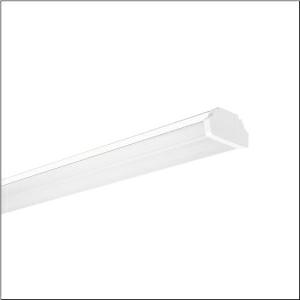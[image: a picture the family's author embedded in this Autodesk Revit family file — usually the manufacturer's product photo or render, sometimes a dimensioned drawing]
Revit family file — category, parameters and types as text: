
# Revit family: dus_r__31_mo_53bd81271v6080_96d5
name_source: partatom
category: Lighting Fixtures
units: mm (PartAtom-declared; Revit-internal decimal feet)

## family parameters
Cut with Voids When Loaded = No
Host = Face
Light Source = No
Part Type = Normal
Room Calculation Point = No
Round Connector Dimension = Use Diameter
Shared = No

## types (1)
- DUS® 31 MO (1 x LED, 7820 lm, 50.8 W, 6500K)
    Apparent Load = 51 VA
    CIE Flux Codes = 47 80 95 92 100
    Color Rendering = 80
    Color Temperature = 6500K
    Default Elevation = 1800 mm
    Description = DUS® 31 MO, luminaire insert, of sheet steel, coil coated, white, length: 1.535mm, width: 81mm, height: 90mm, 5x system unit, system units: 307mm, LED rated luminous flux: 7.820lm, light colour: 865, control gear: ON/OFF, control gear: ECG, with plug, 3-pole, with phase selection, mains connection: 220..240V, AC, 50/60Hz, rated input power: 51W, through-wiring accessed according to module size, primary optical cover: cover, of PMMA, light emission: direct distribution, primary light characteristic: symmetric, protection rating (complete): IP20, protection rating (LED compartment): IP50, insulation class (complete): insulation class I (protective earthing), certification: CE, ENEC, VDE, UKCA, impact resistance: IK03, permissible ambient temperature for indoor applications: -35..+35°C, corresponds to IFS (International Featured Standards) requirements for safety and quality in the food industry, reducing of maximum allowable ambient temperature of 5°C with ceiling mounting, packaging unit: 1 piece
    Height = 95 mm
    Lamp = 1 x LED
    Lamp Light Flux = 7820 lm
    Lamp Power = 50.8 W
    Lamp count = 1
    Length = 1535 mm
    Luminous efficacy = 154 lm/W
    Manufacturer = Siteco
    ModVariant = No
    Model = 53BD81271V6080
    Mounting Place = Ceiling
    Mounting Type = Pendant
    Number of Poles = 1
    OnlyDefault = Yes
    Power Factor = 1
    Product Name = DUS® 31 MO
    Product group = luminaire insert
    ProductGroupID = 901
    Protection Class = Protection class I
    Protection Degree = IP 20
    RLX_Detail_Level = 1
    RLX_Emergency_Light_Flux = 0 lm
    RLX_Emergency_Type = 0
    RLX_Emergency_Type_DB = No
    RlxData = <blob elided: 38433 chars, md5=6a5f2ddc>
    Socket = socket
    Standby Power = 0 W
    System Light Flux = 7820 lm
    System Power = 51 W
    Type Comments = Product without accessories
    Type Image = l_1003451.jpg
    URL = http://relux.com
    VarID = ---
    Voltage = 0 V
    Weight = 0.00 kg
    Width = 81 mm

## geometry (parser evidence)
native form markers: Blend x4, Sweep x11
no freeform markers — native parametric forms only
